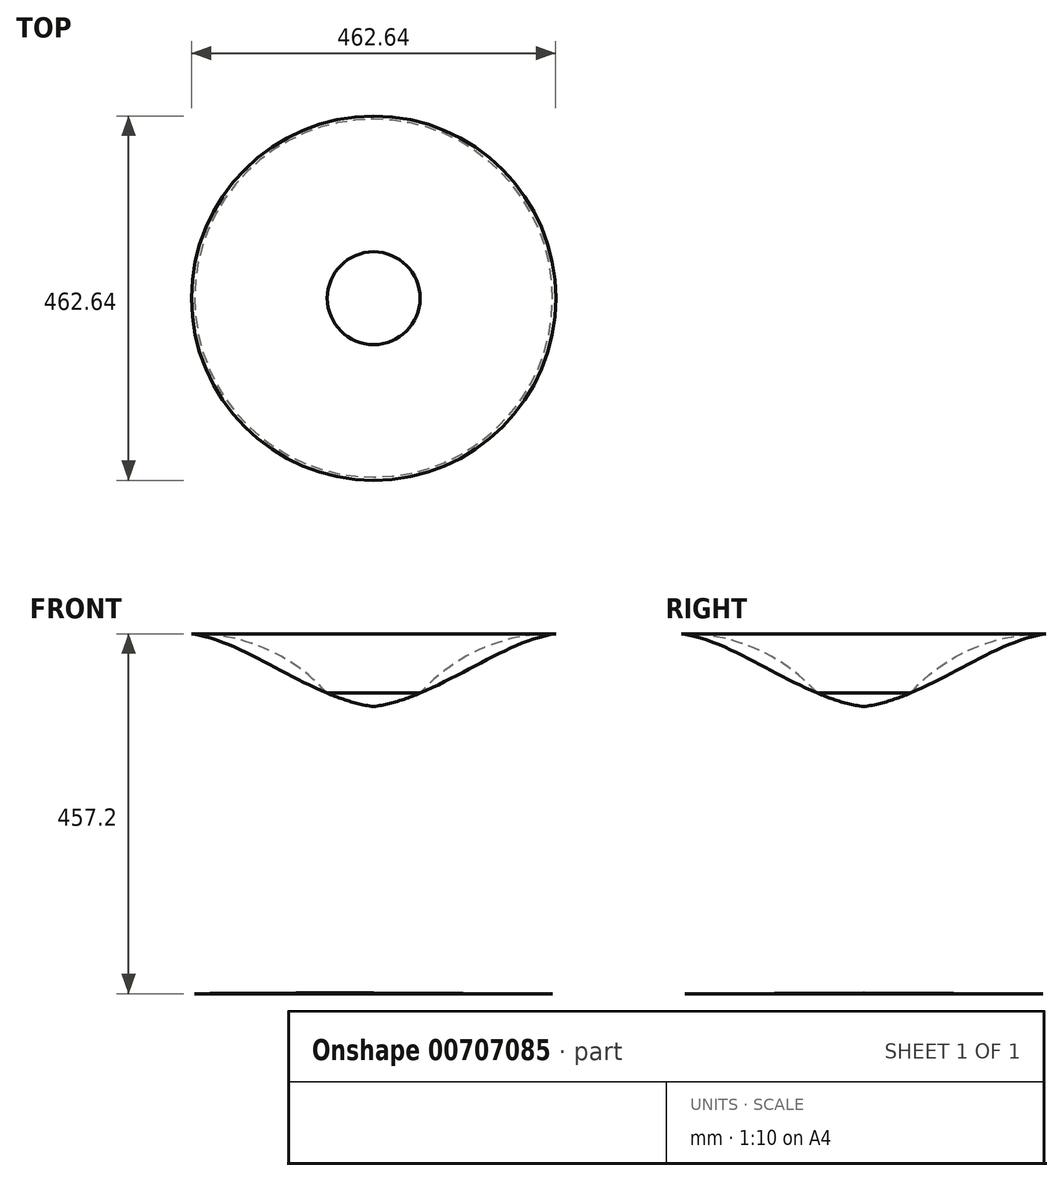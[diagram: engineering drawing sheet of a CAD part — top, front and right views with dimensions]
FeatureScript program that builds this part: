
annotation { "Feature Type Name" : "Feature", "Feature Type Description" : "" }
export const myFeature = defineFeature(function(context is Context, id is Id, definition is map)
    precondition{}
    {
        {
            var Q0;
            Q0=qCreatedBy(makeId("Front.planeOp"),FACE);
            var sketch = newSketch(context, id + "F0", { "sketchPlane" : qUnion([Q0])});
            skCircle(sketch, "E0", {"center": v(-228.6, 0) * mm, "radius": 228.6 * mm});
            skPoint(sketch, "E0.first.point", {"position": v(0, 0) * mm});
            skPoint(sketch, "E0.second.point", {"position": v(-457.2, 0) * mm});
            skPoint(sketch, "E0.third.point", {"position": v(-216.9, 228.3) * mm});
            skLineSegment(sketch, "E1", {"start": v(0, 136.11) * mm, "end": v(0, -227.33) * mm});
            skCircle(sketch, "E2.MirrorC", {"center": v(228.6, 0) * mm, "radius": 228.6 * mm});
            skLineSegment(sketch, "E3", {"start": v(-263.88, -225.86) * mm, "end": v(227.33, -228.6) * mm});
            skFitSpline(sketch, "E4", {"points": [v(-216.9, 228.3) * mm, v(0, 136.11) * mm, v(231.32, 228.58) * mm, v(385.24, 166.5) * mm], "startDerivative": vector(606.93, -436.9) * mm, "endDerivative": vector(495.25, -357.74) * mm});
            skSolve(sketch);
        }
        {
            var Q0;
            {var subQ0=sQuery(id+"F0.wireOp",EDGE,"E4");var subQ1=sQuery(id+"F0.wireOp",EDGE,"E1");var subQ2=makeQuery(id+"F0.imprint","INTERSECT",VERTEX,{"derivedFrom":[subQ1,subQ0]});Q0=makeQuery(id+"F0.imprint","IMPRINT",FACE,{"disambiguationData":[TD([[makeQuery(id+"F0.imprint","IMPRINT",EDGE,{"disambiguationData":[TD([[subQ2,-1.0]])],"derivedFrom":subQ0}),-1.0]])]});}
            var Q1;
            {var subQ0=sQuery(id+"F0.wireOp",EDGE,"E3");var subQ1=sQuery(id+"F0.wireOp",EDGE,"E1");var subQ2=makeQuery(id+"F0.imprint","INTERSECT",VERTEX,{"derivedFrom":[subQ1,subQ0]});Q1=makeQuery(id+"F0.imprint","IMPRINT",FACE,{"disambiguationData":[TD([[makeQuery(id+"F0.imprint","IMPRINT",EDGE,{"disambiguationData":[TD([[subQ2,-1.0]])],"derivedFrom":subQ0}),1.0]])]});}
            var Q2;
            {var subQ0=sQuery(id+"F0.wireOp",EDGE,"E4");var subQ1=sQuery(id+"F0.wireOp",EDGE,"E2.MirrorC");var subQ2=makeQuery(id+"F0.imprint","INTERSECT",VERTEX,{"disambiguationData":[OD(0.0)],"derivedFrom":[subQ1,subQ0]});Q2=makeQuery(id+"F0.imprint","IMPRINT",FACE,{"disambiguationData":[TD([[makeQuery(id+"F0.imprint","IMPRINT",EDGE,{"disambiguationData":[TD([[subQ2,1.0]])],"derivedFrom":subQ1}),-1.0]])]});}
            var Q3;
            {var subQ0=sQuery(id+"F0.wireOp",EDGE,"E2.MirrorC");var subQ3=sQuery(id+"F0.wireOp",EDGE,"E4");var subQ5=makeQuery(id+"F0.imprint","INTERSECT",VERTEX,{"disambiguationData":[OD(2.0)],"derivedFrom":[subQ0,subQ3]});Q3=makeQuery(id+"F0.imprint","IMPRINT",FACE,{"disambiguationData":[TD([[makeQuery(id+"F0.imprint","IMPRINT",EDGE,{"disambiguationData":[TD([[subQ5,-1.0]])],"derivedFrom":subQ0}),-1.0]])]});}
            var Q4;
            {var subQ0=sQuery(id+"F0.wireOp",EDGE,"E4");var subQ1=sQuery(id+"F0.wireOp",EDGE,"E2.MirrorC");var subQ2=makeQuery(id+"F0.imprint","INTERSECT",VERTEX,{"disambiguationData":[OD(2.0)],"derivedFrom":[subQ1,subQ0]});Q4=makeQuery(id+"F0.imprint","IMPRINT",FACE,{"disambiguationData":[TD([[makeQuery(id+"F0.imprint","IMPRINT",EDGE,{"disambiguationData":[TD([[subQ2,-1.0]])],"derivedFrom":subQ1}),1.0]])]});}
            var Q5;
            Q5=sQuery(id+"F0.wireOp",EDGE,"E1");
            revolve(context, id + "F1", {"entities" : qUnion([Q0, Q1, Q2, Q3, Q4]), "axis" : qUnion([Q5]), "revolveType" : RevolveType.FULL});
        }
    });
